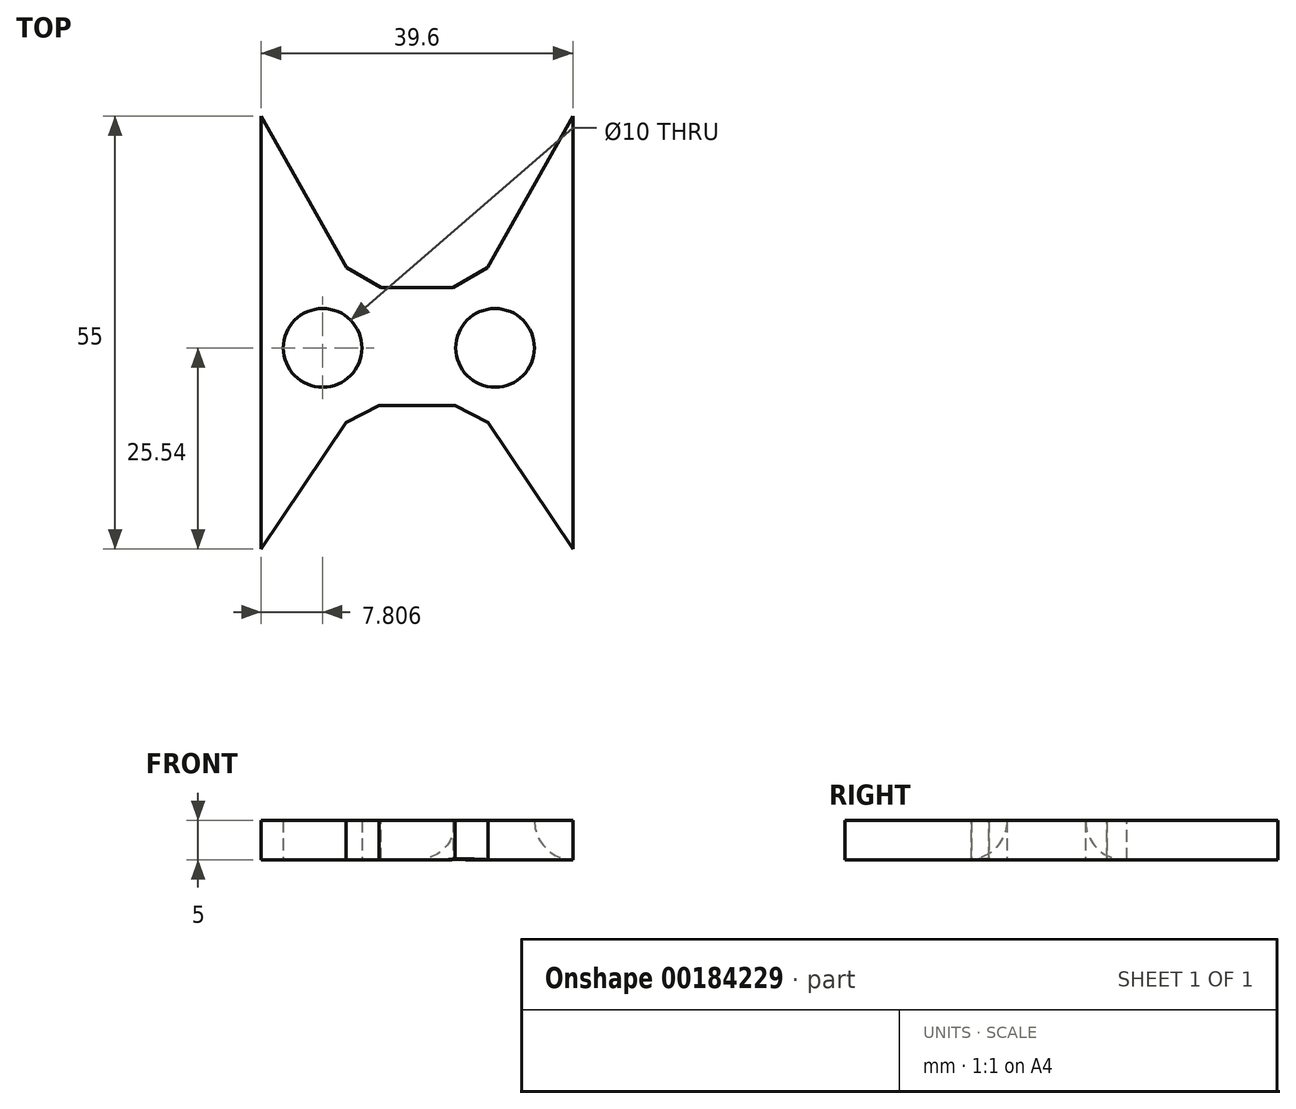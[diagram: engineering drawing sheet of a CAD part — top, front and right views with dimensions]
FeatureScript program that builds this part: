
annotation { "Feature Type Name" : "Feature", "Feature Type Description" : "" }
export const myFeature = defineFeature(function(context is Context, id is Id, definition is map)
    precondition{}
    {
        {
            var Q0;
            Q0=qCreatedBy(makeId("Top.planeOp"),FACE);
            var sketch = newSketch(context, id + "F0", { "sketchPlane" : qUnion([Q0])});
            skLineSegment(sketch, "E0", {"start": v(-22.41, 7.7) * mm, "end": v(-7.41, 7.7) * mm});
            skLineSegment(sketch, "E1", {"start": v(-22.41, -7.3) * mm, "end": v(-7.41, -7.3) * mm});
            skLineSegment(sketch, "E2", {"start": v(-7.41, 7.7) * mm, "end": v(4.9, 29.46) * mm});
            skLineSegment(sketch, "E3", {"start": v(4.9, 29.46) * mm, "end": v(4.9, -25.54) * mm});
            skLineSegment(sketch, "E4", {"start": v(4.9, -25.54) * mm, "end": v(-7.41, -7.3) * mm});
            skLineSegment(sketch, "E5", {"start": v(-22.41, -7.3) * mm, "end": v(-34.71, -25.54) * mm});
            skLineSegment(sketch, "E6", {"start": v(-34.71, -25.54) * mm, "end": v(-34.71, 29.46) * mm});
            skLineSegment(sketch, "E7", {"start": v(-34.71, 29.46) * mm, "end": v(-22.41, 7.7) * mm});
            skCircle(sketch, "E8", {"center": v(-26.9, 0) * mm, "radius": 5 * mm});
            skCircle(sketch, "E9", {"center": v(-5, 0) * mm, "radius": 5 * mm});
            skSolve(sketch);
        }
        {
            var Q0;
            Q0 = qSketchRegion(id + "F0", true);
            extrude(context, id + "F1", {"entities" : qUnion([Q0]), "depth" : 5 * mm});
        }
        {
            var Q0;
            Q0=makeQuery(id+"F1.opExtrude","SWEPT_EDGE",EDGE,{"disambiguationData":[OSD([sQuery(id+"F0.wireOp",EDGE,"E0"),sQuery(id+"F0.wireOp",EDGE,"E7")])]});
            var Q1;
            Q1=makeQuery(id+"F1.opExtrude","SWEPT_EDGE",EDGE,{"disambiguationData":[OSD([sQuery(id+"F0.wireOp",EDGE,"E0"),sQuery(id+"F0.wireOp",EDGE,"E2")])]});
            var Q2;
            Q2=makeQuery(id+"F1.opExtrude","SWEPT_EDGE",EDGE,{"disambiguationData":[OSD([sQuery(id+"F0.wireOp",EDGE,"E1"),sQuery(id+"F0.wireOp",EDGE,"E5")])]});
            var Q3;
            Q3=makeQuery(id+"F1.opExtrude","SWEPT_EDGE",EDGE,{"disambiguationData":[OSD([sQuery(id+"F0.wireOp",EDGE,"E1"),sQuery(id+"F0.wireOp",EDGE,"E4")])]});
            chamfer(context, id + "F2", {"entities" : qUnion([Q0, Q1, Q2, Q3]), "width" : 5 * mm, "tangentPropagation" : true});
        }
        {
            var Q0;
            Q0=makeQuery(id+"F1.opExtrude","CAP_EDGE",EDGE,{"disambiguationData":[OSD([sQuery(id+"F0.wireOp",EDGE,"E9")])],"isStart":true});
            fillet(context, id + "F3", {"entities" : qUnion([Q0]), "radius" : 5 * mm, "tangentPropagation" : true, "allowEdgeOverflow" : false});
        }
    });
